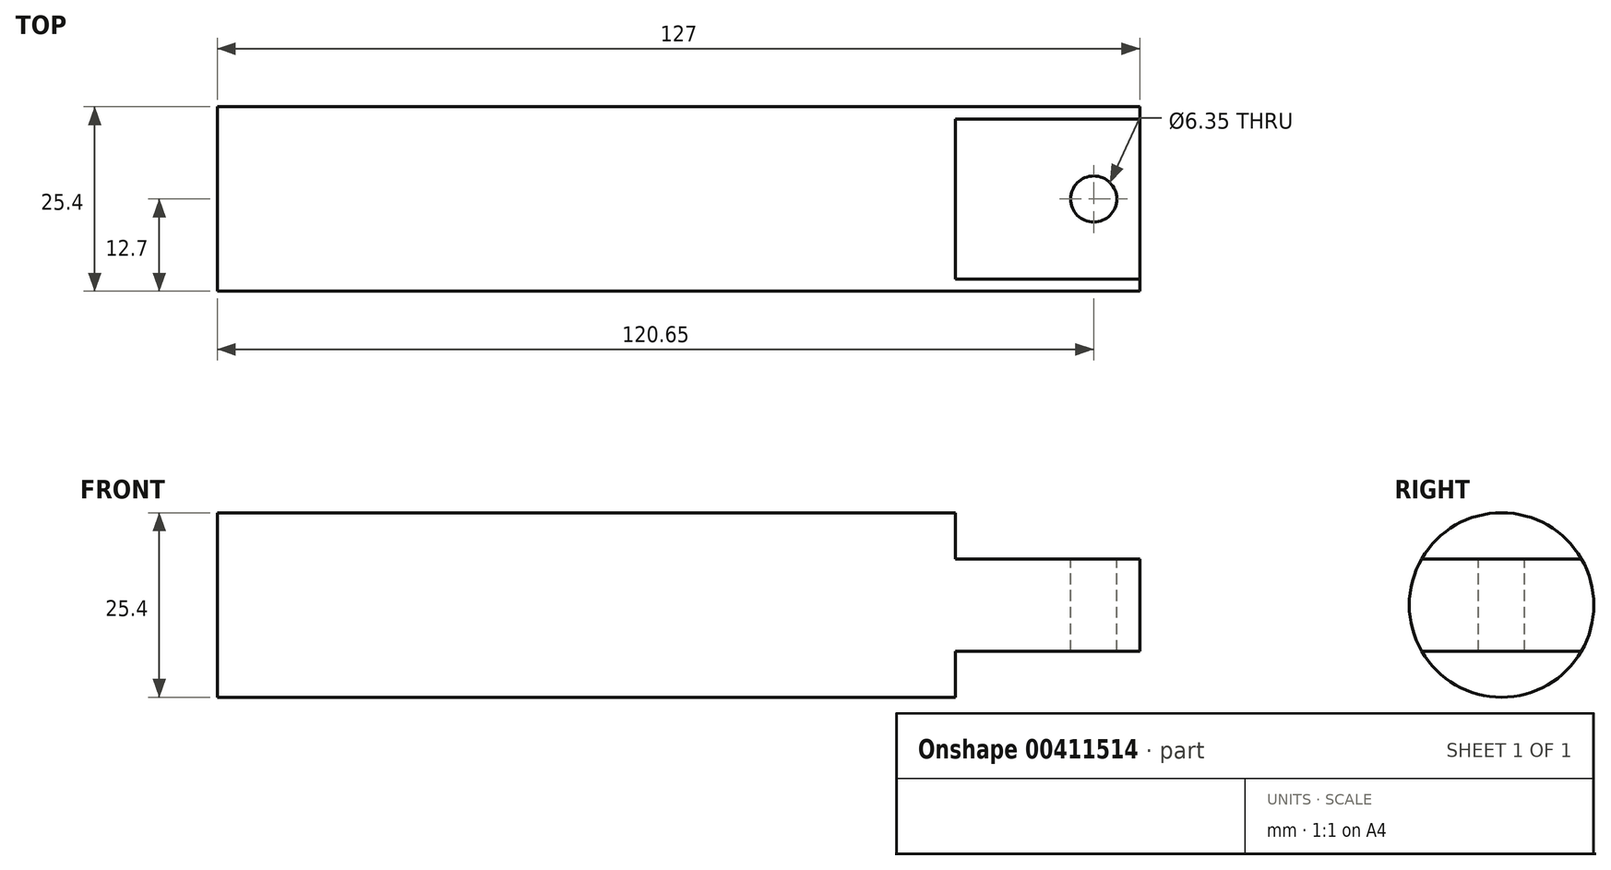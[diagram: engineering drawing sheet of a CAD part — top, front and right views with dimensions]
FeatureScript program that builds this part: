
annotation { "Feature Type Name" : "Feature", "Feature Type Description" : "" }
export const myFeature = defineFeature(function(context is Context, id is Id, definition is map)
    precondition{}
    {
        {
            var Q0;
            Q0=qCreatedBy(makeId("Right.planeOp"),FACE);
            var sketch = newSketch(context, id + "F0", { "sketchPlane" : qUnion([Q0])});
            skCircle(sketch, "E0", {"center": v(0, 0) * mm, "radius": 12.7 * mm});
            skSolve(sketch);
        }
        {
            var Q0;
            Q0 = qSketchRegion(id + "F0", true);
            extrude(context, id + "F1", {"entities" : qUnion([Q0]), "endBound" : BoundingType.SYMMETRIC, "depth" : 127 * mm});
        }
        {
            var Q0;
            Q0=makeQuery(id+"F1.opExtrude","CAP_FACE",FACE,{"disambiguationData":[OSD([sQuery(id+"F0.wireOp",EDGE,"E0")])],"isStart":false});
            var sketch = newSketch(context, id + "F2", { "sketchPlane" : qUnion([Q0])});
            skArc(sketch, "E1", {"start": v(-11, -6.35) * mm, "mid": v(0, -12.7) * mm, "end": v(11, -6.35) * mm});
            skLineSegment(sketch, "E2", {"start": v(-12.7, 0) * mm, "end": v(12.7, 0) * mm, "construction": true});
            skLineSegment(sketch, "E3", {"start": v(-11, 6.35) * mm, "end": v(11, 6.35) * mm});
            skLineSegment(sketch, "E4.MirrorCS", {"start": v(-11, -6.35) * mm, "end": v(11, -6.35) * mm});
            skArc(sketch, "E5.trimOffspring", {"start": v(11, 6.35) * mm, "mid": v(0, 12.7) * mm, "end": v(-11, 6.35) * mm});
            skSolve(sketch);
        }
        {
            var Q0;
            Q0 = qSketchRegion(id + "F2", true);
            extrude(context, id + "F3", {"entities" : qUnion([Q0]), "operationType" : NewBodyOperationType.REMOVE, "oppositeDirection" : true, "depth" : 25.4 * mm});
        }
        {
            var Q0;
            Q0=makeQuery(id+"F3.boolean.opBoolean","COPY",FACE,{"derivedFrom":makeQuery(id+"F3.opExtrude","SWEPT_FACE",FACE,{"disambiguationData":[OSD([sQuery(id+"F2.wireOp",EDGE,"E3")])]})});
            var sketch = newSketch(context, id + "F4", { "sketchPlane" : qUnion([Q0])});
            skCircle(sketch, "E6", {"center": v(57.15, 0) * mm, "radius": 3.18 * mm});
            skSolve(sketch);
        }
        {
            var Q0;
            Q0=makeQuery(id+"F4.imprint","IMPRINT",FACE,{"disambiguationData":[TD([[makeQuery(id+"F4.imprint","IMPRINT",EDGE,{"derivedFrom":sQuery(id+"F4.wireOp",EDGE,"E6")}),1.0]])]});
            extrude(context, id + "F5", {"entities" : qUnion([Q0]), "operationType" : NewBodyOperationType.REMOVE, "endBound" : BoundingType.THROUGH_ALL, "oppositeDirection" : true, "depth" : 25.4 * mm});
        }
    });
